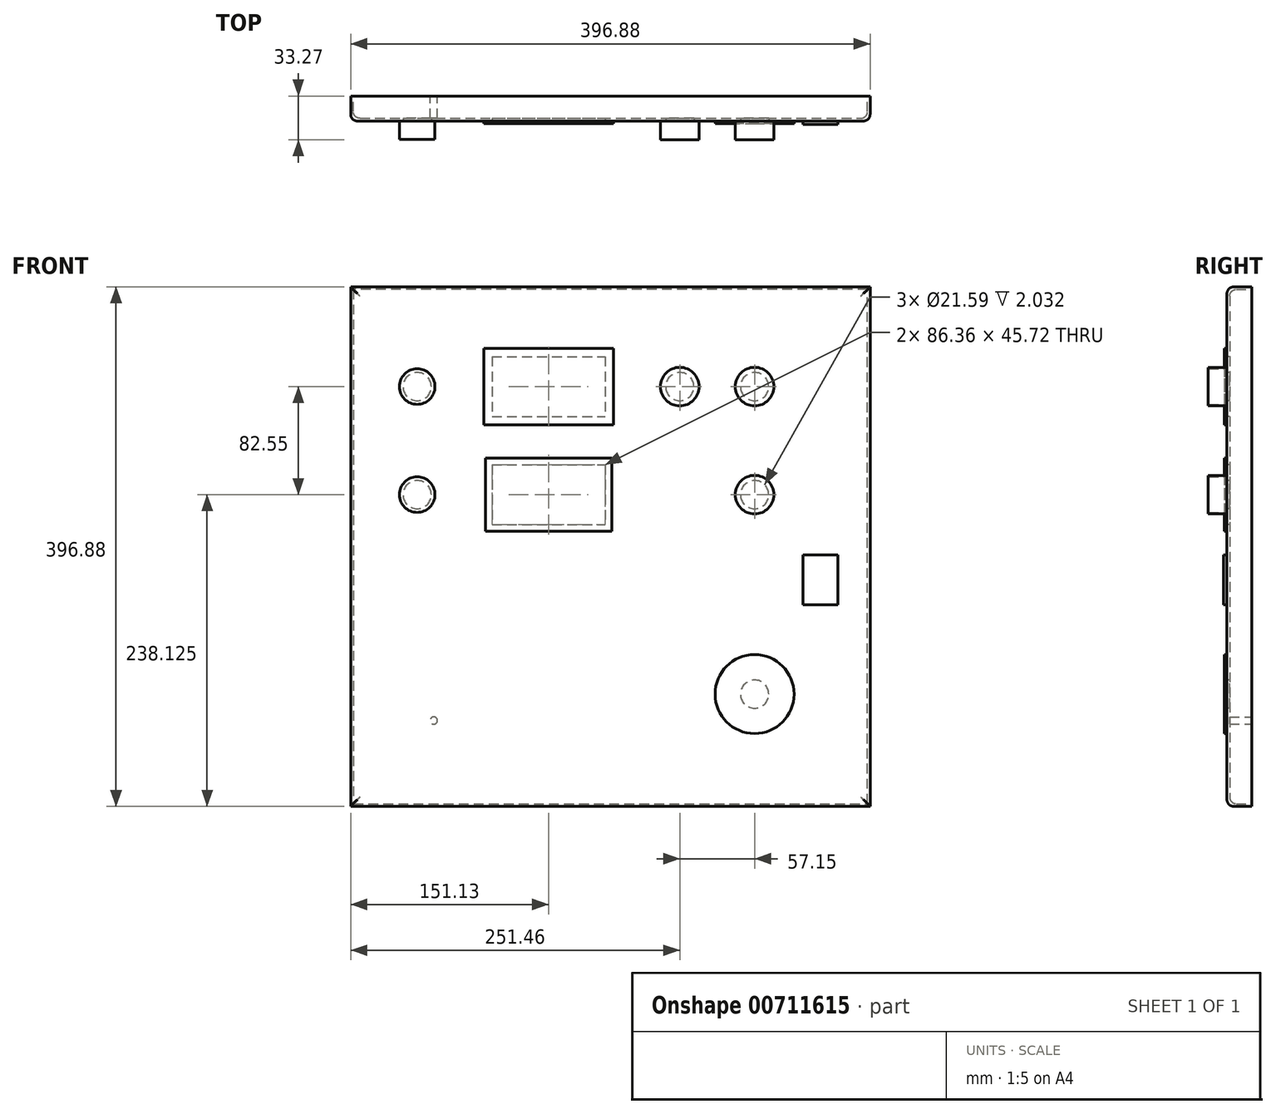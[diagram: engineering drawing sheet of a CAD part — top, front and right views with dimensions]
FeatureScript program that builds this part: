
annotation { "Feature Type Name" : "Feature", "Feature Type Description" : "" }
export const myFeature = defineFeature(function(context is Context, id is Id, definition is map)
    precondition{}
    {
        {
            var Q0;
            Q0=qCreatedBy(makeId("Front.planeOp"),FACE);
            var sketch = newSketch(context, id + "F0", { "sketchPlane" : qUnion([Q0])});
            skLineSegment(sketch, "E0.bottom", {"start": v(0, 0) * mm, "end": v(396.88, 0) * mm});
            skLineSegment(sketch, "E0.top", {"start": v(0, 396.88) * mm, "end": v(396.88, 396.88) * mm});
            skLineSegment(sketch, "E0.left", {"start": v(0, 0) * mm, "end": v(0, 396.88) * mm});
            skLineSegment(sketch, "E0.right", {"start": v(396.88, 0) * mm, "end": v(396.88, 396.88) * mm});
            skSolve(sketch);
        }
        {
            var Q0;
            Q0 = qSketchRegion(id + "F0", true);
            extrude(context, id + "F1", {"entities" : qUnion([Q0]), "depth" : 19.05 * mm, "offsetDistance" : 25.4 * mm});
        }
        {
            var Q0;
            Q0=qCreatedBy(makeId("Front.planeOp"),FACE);
            var sketch = newSketch(context, id + "F2", { "sketchPlane" : qUnion([Q0])});
            skLineSegment(sketch, "E1.0", {"start": v(394.84, 394.84) * mm, "end": v(2.03, 394.84) * mm});
            skLineSegment(sketch, "E1.1", {"start": v(394.84, 2.03) * mm, "end": v(394.84, 394.84) * mm});
            skLineSegment(sketch, "E1.2", {"start": v(2.03, 2.03) * mm, "end": v(394.84, 2.03) * mm});
            skLineSegment(sketch, "E1.3", {"start": v(2.03, 394.84) * mm, "end": v(2.03, 2.03) * mm});
            skSolve(sketch);
        }
        {
            var Q0;
            Q0 = qSketchRegion(id + "F2", true);
            extrude(context, id + "F3", {"entities" : qUnion([Q0]), "operationType" : NewBodyOperationType.REMOVE, "depth" : 17.02 * mm, "offsetDistance" : 25.4 * mm});
        }
        {
            var Q0;
            Q0=makeQuery(id+"F1.opExtrude","CAP_FACE",FACE,{"disambiguationData":[OSD([sQuery(id+"F0.wireOp",EDGE,"E0.bottom"),sQuery(id+"F0.wireOp",EDGE,"E0.top"),sQuery(id+"F0.wireOp",EDGE,"E0.left"),sQuery(id+"F0.wireOp",EDGE,"E0.right")])],"isStart":false});
            fillet(context, id + "F4", {"entities" : qUnion([Q0]), "radius" : 5.08 * mm, "tangentPropagation" : true, "allowEdgeOverflow" : false});
        }
        {
            var Q0;
            Q0=makeQuery(id+"F3.boolean.opBoolean","COPY",FACE,{"derivedFrom":makeQuery(id+"F3.opExtrude","CAP_FACE",FACE,{"disambiguationData":[OSD([sQuery(id+"F2.wireOp",EDGE,"E1.0"),sQuery(id+"F2.wireOp",EDGE,"E1.1"),sQuery(id+"F2.wireOp",EDGE,"E1.2"),sQuery(id+"F2.wireOp",EDGE,"E1.3")])],"isStart":false})});
            fillet(context, id + "F5", {"entities" : qUnion([Q0]), "radius" : 5.08 * mm, "tangentPropagation" : true, "allowEdgeOverflow" : false});
        }
        {
            var Q0;
            Q0=qCreatedBy(makeId("Front.planeOp"),FACE);
            var sketch = newSketch(context, id + "F6", { "sketchPlane" : qUnion([Q0])});
            skCircle(sketch, "E2", {"center": v(63.5, 65.53) * mm, "radius": 2.8 * mm});
            skSolve(sketch);
        }
        {
            var Q0;
            Q0 = qSketchRegion(id + "F6", true);
            extrude(context, id + "F7", {"entities" : qUnion([Q0]), "operationType" : NewBodyOperationType.ADD, "endBound" : BoundingType.UP_TO_NEXT, "depth" : 25.4 * mm, "offsetDistance" : 25.4 * mm});
        }
        {
            var Q0;
            Q0=makeQuery(id+"F1.opExtrude","CAP_FACE",FACE,{"disambiguationData":[OSD([sQuery(id+"F0.wireOp",EDGE,"E0.bottom"),sQuery(id+"F0.wireOp",EDGE,"E0.top"),sQuery(id+"F0.wireOp",EDGE,"E0.left"),sQuery(id+"F0.wireOp",EDGE,"E0.right")])],"isStart":false});
            var sketch = newSketch(context, id + "F8", { "sketchPlane" : qUnion([Q0])});
            skCircle(sketch, "E3", {"center": v(50.8, 320.68) * mm, "radius": 10.8 * mm});
            skCircle(sketch, "E4", {"center": v(50.8, 238.13) * mm, "radius": 10.8 * mm});
            skLineSegment(sketch, "E5", {"start": v(50.8, 320.68) * mm, "end": v(410.29, 320.68) * mm, "construction": true});
            skLineSegment(sketch, "E6", {"start": v(50.8, 238.13) * mm, "end": v(391.8, 238.13) * mm, "construction": true});
            skLineSegment(sketch, "E7.bottom", {"start": v(107.95, 343.54) * mm, "end": v(194.31, 343.54) * mm});
            skLineSegment(sketch, "E7.top", {"start": v(107.95, 297.82) * mm, "end": v(194.31, 297.82) * mm});
            skLineSegment(sketch, "E7.left", {"start": v(107.95, 343.54) * mm, "end": v(107.95, 297.82) * mm});
            skLineSegment(sketch, "E7.right", {"start": v(194.31, 343.54) * mm, "end": v(194.31, 297.82) * mm});
            skLineSegment(sketch, "E8.bottom", {"start": v(107.95, 215.27) * mm, "end": v(194.31, 215.27) * mm});
            skLineSegment(sketch, "E8.top", {"start": v(107.95, 260.99) * mm, "end": v(194.31, 260.99) * mm});
            skLineSegment(sketch, "E8.left", {"start": v(107.95, 260.99) * mm, "end": v(107.95, 215.27) * mm});
            skLineSegment(sketch, "E8.right", {"start": v(194.31, 260.99) * mm, "end": v(194.31, 215.27) * mm});
            skCircle(sketch, "E9", {"center": v(251.46, 320.68) * mm, "radius": 10.8 * mm});
            skCircle(sketch, "E10", {"center": v(308.61, 320.68) * mm, "radius": 10.8 * mm});
            skCircle(sketch, "E11", {"center": v(308.61, 238.13) * mm, "radius": 10.8 * mm});
            skLineSegment(sketch, "E12", {"start": v(151.13, 343.54) * mm, "end": v(151.13, 215.27) * mm, "construction": true});
            skCircle(sketch, "E13", {"center": v(308.61, 85.73) * mm, "radius": 10.8 * mm});
            skCircle(sketch, "E14", {"center": v(111.37, 340.11) * mm, "radius": 3.42 * mm, "construction": true});
            skCircle(sketch, "E15", {"center": v(111.37, 257.56) * mm, "radius": 3.42 * mm, "construction": true});
            skCircle(sketch, "E16", {"center": v(190.89, 257.56) * mm, "radius": 3.42 * mm, "construction": true});
            skCircle(sketch, "E17", {"center": v(190.89, 340.11) * mm, "radius": 3.42 * mm, "construction": true});
            skCircle(sketch, "E18", {"center": v(111.37, 301.24) * mm, "radius": 3.42 * mm, "construction": true});
            skCircle(sketch, "E19", {"center": v(190.89, 301.24) * mm, "radius": 3.42 * mm, "construction": true});
            skCircle(sketch, "E20", {"center": v(111.37, 218.69) * mm, "radius": 3.42 * mm, "construction": true});
            skCircle(sketch, "E21", {"center": v(190.89, 218.69) * mm, "radius": 3.42 * mm, "construction": true});
            skLineSegment(sketch, "E22.0", {"start": v(114.3, 337.19) * mm, "end": v(187.96, 337.19) * mm, "construction": true});
            skLineSegment(sketch, "E22.1", {"start": v(114.3, 337.19) * mm, "end": v(114.3, 304.17) * mm, "construction": true});
            skLineSegment(sketch, "E22.2", {"start": v(114.3, 304.17) * mm, "end": v(187.96, 304.17) * mm, "construction": true});
            skLineSegment(sketch, "E22.3", {"start": v(187.96, 337.19) * mm, "end": v(187.96, 304.17) * mm, "construction": true});
            skLineSegment(sketch, "E23.0", {"start": v(114.3, 254.63) * mm, "end": v(187.96, 254.63) * mm, "construction": true});
            skLineSegment(sketch, "E23.1", {"start": v(114.3, 254.63) * mm, "end": v(114.3, 221.62) * mm, "construction": true});
            skLineSegment(sketch, "E23.2", {"start": v(114.3, 221.62) * mm, "end": v(187.96, 221.62) * mm, "construction": true});
            skLineSegment(sketch, "E23.3", {"start": v(187.96, 254.63) * mm, "end": v(187.96, 221.62) * mm, "construction": true});
            skSolve(sketch);
        }
        {
            var Q0;
            Q0 = qSketchRegion(id + "F8", true);
            extrude(context, id + "F9", {"entities" : qUnion([Q0]), "operationType" : NewBodyOperationType.REMOVE, "endBound" : BoundingType.THROUGH_ALL, "oppositeDirection" : true, "depth" : 25.4 * mm, "offsetDistance" : 25.4 * mm});
        }
        {
            var Q0;
            Q0=makeQuery(id+"F1.opExtrude","CAP_FACE",FACE,{"disambiguationData":[OSD([sQuery(id+"F0.wireOp",EDGE,"E0.bottom"),sQuery(id+"F0.wireOp",EDGE,"E0.top"),sQuery(id+"F0.wireOp",EDGE,"E0.left"),sQuery(id+"F0.wireOp",EDGE,"E0.right")])],"isStart":false});
            var sketch = newSketch(context, id + "F10", { "sketchPlane" : qUnion([Q0])});
            skCircle(sketch, "E24", {"center": v(50.8, 320.68) * mm, "radius": 13.59 * mm});
            skCircle(sketch, "E25", {"center": v(50.8, 238.13) * mm, "radius": 13.59 * mm});
            skSolve(sketch);
        }
        {
            var Q0;
            Q0 = qSketchRegion(id + "F10", true);
            extrude(context, id + "F11", {"entities" : qUnion([Q0]), "depth" : 13.97 * mm, "offsetDistance" : 25.4 * mm});
        }
        {
            var Q0;
            Q0=makeQuery(id+"F1.opExtrude","CAP_FACE",FACE,{"disambiguationData":[OSD([sQuery(id+"F0.wireOp",EDGE,"E0.bottom"),sQuery(id+"F0.wireOp",EDGE,"E0.top"),sQuery(id+"F0.wireOp",EDGE,"E0.left"),sQuery(id+"F0.wireOp",EDGE,"E0.right")])],"isStart":false});
            var sketch = newSketch(context, id + "F12", { "sketchPlane" : qUnion([Q0])});
            skLineSegment(sketch, "E26.0", {"start": v(200.66, 349.88) * mm, "end": v(200.66, 291.47) * mm});
            skLineSegment(sketch, "E26.1", {"start": v(101.6, 349.89) * mm, "end": v(200.66, 349.89) * mm});
            skLineSegment(sketch, "E26.2", {"start": v(101.6, 349.88) * mm, "end": v(101.6, 291.47) * mm});
            skLineSegment(sketch, "E26.3", {"start": v(101.6, 291.47) * mm, "end": v(200.66, 291.47) * mm});
            skLineSegment(sketch, "E27.0", {"start": v(102.87, 266.06) * mm, "end": v(199.4, 266.06) * mm});
            skLineSegment(sketch, "E27.1", {"start": v(102.87, 266.06) * mm, "end": v(102.87, 210.19) * mm});
            skLineSegment(sketch, "E27.2", {"start": v(102.87, 210.19) * mm, "end": v(199.4, 210.19) * mm});
            skLineSegment(sketch, "E27.3", {"start": v(199.4, 266.06) * mm, "end": v(199.4, 210.19) * mm});
            skSolve(sketch);
        }
        {
            var Q0;
            Q0 = qSketchRegion(id + "F12", true);
            extrude(context, id + "F13", {"entities" : qUnion([Q0]), "depth" : 2.03 * mm, "offsetDistance" : 25.4 * mm});
        }
        {
            var Q0;
            Q0=makeQuery(id+"F1.opExtrude","CAP_FACE",FACE,{"disambiguationData":[OSD([sQuery(id+"F0.wireOp",EDGE,"E0.bottom"),sQuery(id+"F0.wireOp",EDGE,"E0.top"),sQuery(id+"F0.wireOp",EDGE,"E0.left"),sQuery(id+"F0.wireOp",EDGE,"E0.right")])],"isStart":false});
            var sketch = newSketch(context, id + "F14", { "sketchPlane" : qUnion([Q0])});
            skCircle(sketch, "E28.0", {"center": v(251.46, 320.68) * mm, "radius": 14.73 * mm});
            skCircle(sketch, "E29.0", {"center": v(308.61, 320.68) * mm, "radius": 14.73 * mm});
            skCircle(sketch, "E30.0", {"center": v(308.61, 238.13) * mm, "radius": 14.73 * mm});
            skSolve(sketch);
        }
        {
            var Q0;
            Q0 = qSketchRegion(id + "F14", true);
            extrude(context, id + "F15", {"entities" : qUnion([Q0]), "operationType" : NewBodyOperationType.ADD, "depth" : 14.22 * mm, "offsetDistance" : 25.4 * mm});
        }
        {
            var Q0;
            Q0=makeQuery(id+"F1.opExtrude","CAP_FACE",FACE,{"disambiguationData":[OSD([sQuery(id+"F0.wireOp",EDGE,"E0.bottom"),sQuery(id+"F0.wireOp",EDGE,"E0.top"),sQuery(id+"F0.wireOp",EDGE,"E0.left"),sQuery(id+"F0.wireOp",EDGE,"E0.right")])],"isStart":false});
            var sketch = newSketch(context, id + "F16", { "sketchPlane" : qUnion([Q0])});
            skCircle(sketch, "E31", {"center": v(308.61, 85.73) * mm, "radius": 30.16 * mm});
            skSolve(sketch);
        }
        {
            var Q0;
            Q0 = qSketchRegion(id + "F16", true);
            extrude(context, id + "F17", {"entities" : qUnion([Q0]), "depth" : 1.85 * mm, "offsetDistance" : 25.4 * mm});
        }
        {
            var Q0;
            Q0=makeQuery(id+"F1.opExtrude","CAP_FACE",FACE,{"disambiguationData":[OSD([sQuery(id+"F0.wireOp",EDGE,"E0.bottom"),sQuery(id+"F0.wireOp",EDGE,"E0.top"),sQuery(id+"F0.wireOp",EDGE,"E0.left"),sQuery(id+"F0.wireOp",EDGE,"E0.right")])],"isStart":false});
            var sketch = newSketch(context, id + "F18", { "sketchPlane" : qUnion([Q0])});
            skLineSegment(sketch, "E32.bottom", {"start": v(345.44, 153.99) * mm, "end": v(372.1, 153.99) * mm});
            skLineSegment(sketch, "E32.top", {"start": v(345.44, 192.09) * mm, "end": v(372.1, 192.09) * mm});
            skLineSegment(sketch, "E32.left", {"start": v(372.11, 192.09) * mm, "end": v(372.11, 153.99) * mm});
            skLineSegment(sketch, "E32.right", {"start": v(345.44, 192.09) * mm, "end": v(345.44, 153.99) * mm});
            skLineSegment(sketch, "E33", {"start": v(345.44, 173.04) * mm, "end": v(372.1, 173.04) * mm, "construction": true});
            skLineSegment(sketch, "E34", {"start": v(358.78, 192.09) * mm, "end": v(358.78, 153.99) * mm, "construction": true});
            skSolve(sketch);
        }
        {
            var Q0;
            Q0 = qSketchRegion(id + "F18", true);
            extrude(context, id + "F19", {"entities" : qUnion([Q0]), "operationType" : NewBodyOperationType.ADD, "depth" : 2.54 * mm, "offsetDistance" : 25.4 * mm});
        }
    });
